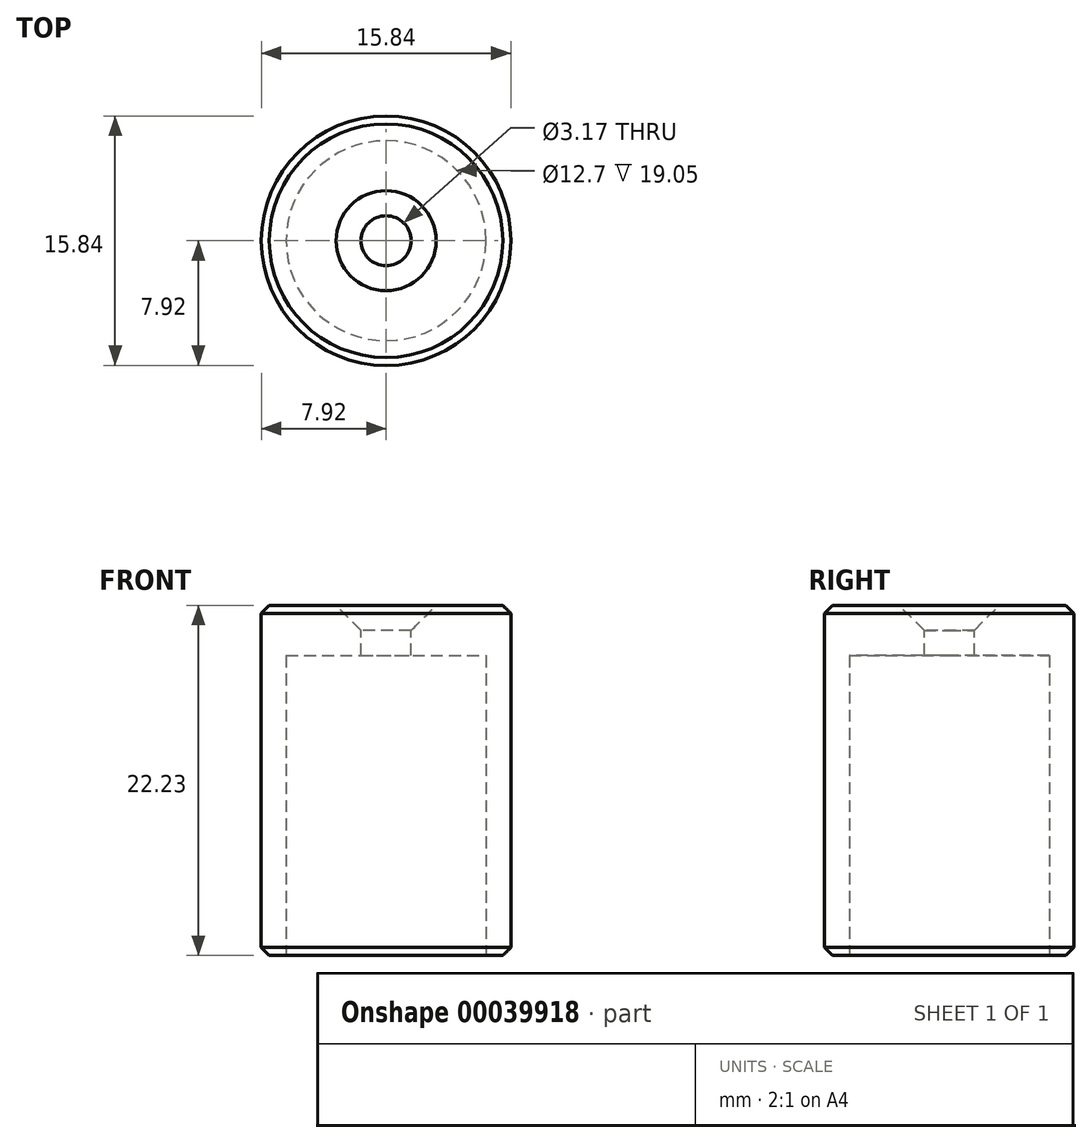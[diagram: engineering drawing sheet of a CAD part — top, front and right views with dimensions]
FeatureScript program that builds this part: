
annotation { "Feature Type Name" : "Feature", "Feature Type Description" : "" }
export const myFeature = defineFeature(function(context is Context, id is Id, definition is map)
    precondition{}
    {
        {
            var Q0;
            Q0=qCreatedBy(makeId("Top.planeOp"),FACE);
            var sketch = newSketch(context, id + "F0", { "sketchPlane" : qUnion([Q0])});
            skCircle(sketch, "E0", {"center": v(0, 0) * mm, "radius": 7.92 * mm});
            skSolve(sketch);
        }
        {
            var Q0;
            Q0 = qSketchRegion(id + "F0", true);
            extrude(context, id + "F1", {"entities" : qUnion([Q0]), "oppositeDirection" : true, "depth" : 22.22 * mm});
        }
        {
            var Q0;
            Q0=makeQuery(id+"F1.opExtrude","CAP_FACE",FACE,{"disambiguationData":[OSD([sQuery(id+"F0.wireOp",EDGE,"E0")])],"isStart":true});
            var sketch = newSketch(context, id + "F2", { "sketchPlane" : qUnion([Q0])});
            skPoint(sketch, "E1", {"position": v(0, 0) * mm});
            skSolve(sketch);
        }
        {
            var Q0;
            Q0=sQuery(id+"F2.wireOp",VERTEX,"E1");
            var Q1;
            Q1=makeQuery(id+"F1.opExtrude","SWEPT_BODY",BODY,{"disambiguationData":[OSD([sQuery(id+"F0.wireOp",EDGE,"E0")])]});
            hole(context, id + "F3", {"style" : HoleStyle.C_SINK, "holeDiameter" : 3.17 * mm, "cSinkDiameter" : 6.35 * mm, "endStyle" : HoleEndStyle.THROUGH, "locations" : qUnion([Q0]), "scope" : qUnion([Q1]), "cSinkAngle" : 90 * degree});
        }
        {
            var Q0;
            Q0=makeQuery(id+"F1.opExtrude","CAP_FACE",FACE,{"disambiguationData":[OSD([sQuery(id+"F0.wireOp",EDGE,"E0")])],"isStart":false});
            var sketch = newSketch(context, id + "F4", { "sketchPlane" : qUnion([Q0])});
            skCircle(sketch, "E2", {"center": v(0, 0) * mm, "radius": 6.35 * mm});
            skSolve(sketch);
        }
        {
            var Q0;
            Q0 = qSketchRegion(id + "F4", true);
            extrude(context, id + "F5", {"entities" : qUnion([Q0]), "operationType" : NewBodyOperationType.REMOVE, "oppositeDirection" : true, "depth" : 19.05 * mm});
        }
        {
            var Q0;
            Q0=makeQuery(id+"F1.opExtrude","CAP_EDGE",EDGE,{"disambiguationData":[OSD([sQuery(id+"F0.wireOp",EDGE,"E0")])],"isStart":true});
            chamfer(context, id + "F6", {"entities" : qUnion([Q0]), "width" : 0.5 * mm, "tangentPropagation" : true});
        }
        {
            var Q0;
            Q0=makeQuery(id+"F1.opExtrude","CAP_EDGE",EDGE,{"disambiguationData":[OSD([sQuery(id+"F0.wireOp",EDGE,"E0")])],"isStart":false});
            chamfer(context, id + "F7", {"entities" : qUnion([Q0]), "width" : 0.5 * mm, "tangentPropagation" : true});
        }
    });
